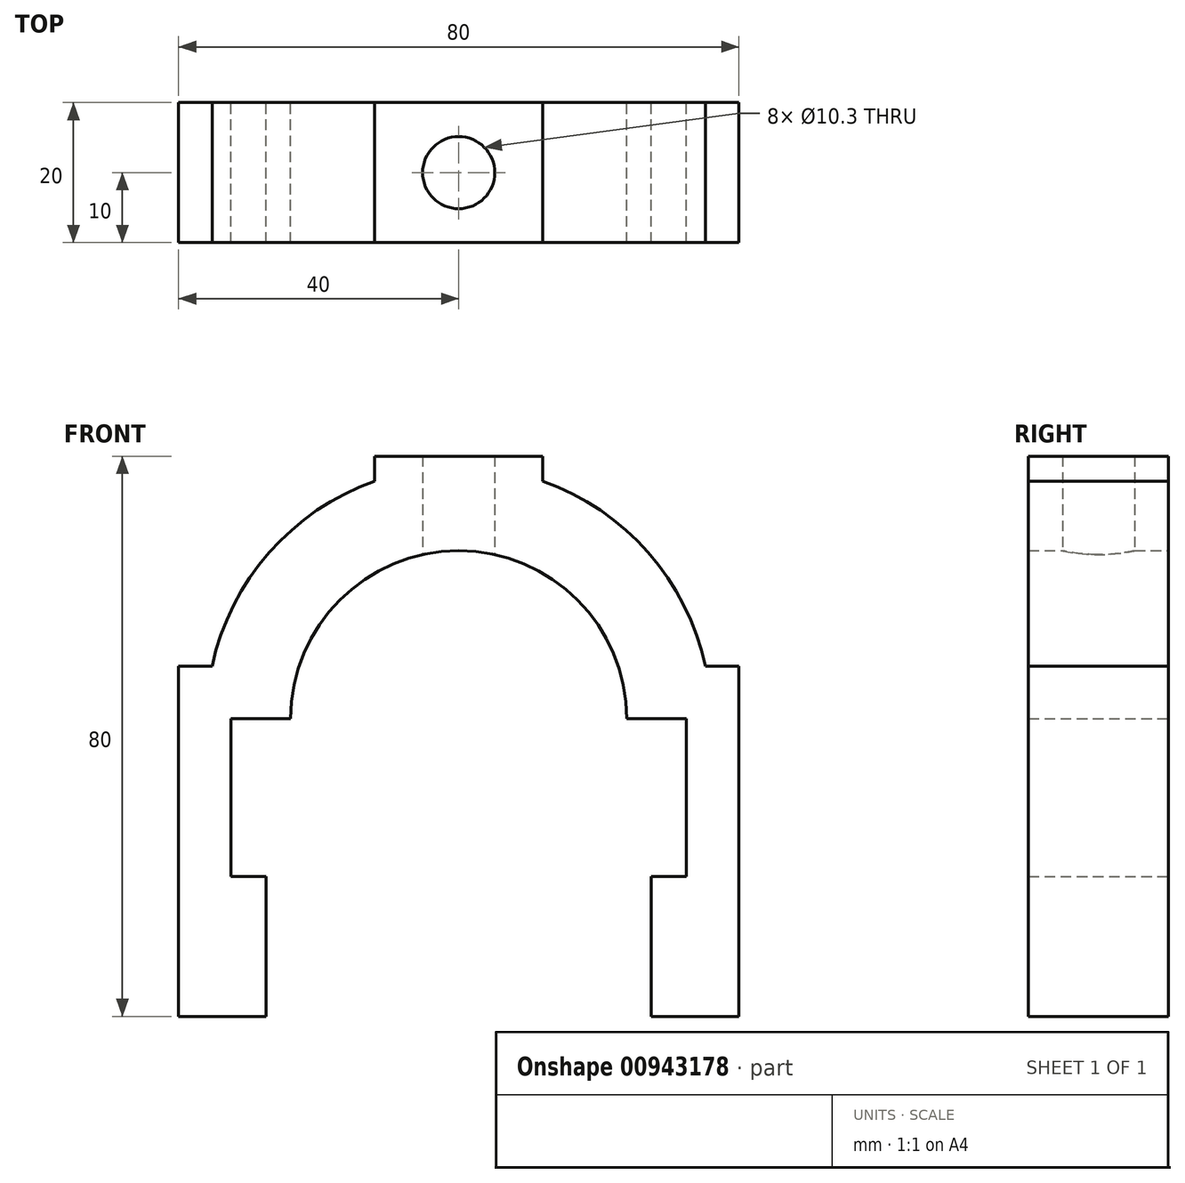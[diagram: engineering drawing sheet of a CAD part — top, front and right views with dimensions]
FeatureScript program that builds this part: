
annotation { "Feature Type Name" : "Feature", "Feature Type Description" : "" }
export const myFeature = defineFeature(function(context is Context, id is Id, definition is map)
    precondition{}
    {
        {
            var Q0;
            Q0=qCreatedBy(makeId("Front.planeOp"),FACE);
            var sketch = newSketch(context, id + "F0", { "sketchPlane" : qUnion([Q0])});
            skLineSegment(sketch, "E0", {"start": v(0, 51.15) * mm, "end": v(0, -47.63) * mm, "construction": true});
            skArc(sketch, "E1", {"start": v(-12, 33.94) * mm, "mid": v(-27.06, 23.75) * mm, "end": v(-35.21, 7.5) * mm});
            skArc(sketch, "E2", {"start": v(0, 24) * mm, "mid": v(-16.97, 16.97) * mm, "end": v(-24, 0) * mm});
            skLineSegment(sketch, "E3", {"start": v(-40, -42.5) * mm, "end": v(-27.5, -42.5) * mm});
            skLineSegment(sketch, "E4", {"start": v(-27.5, -42.5) * mm, "end": v(-27.5, -22.5) * mm});
            skLineSegment(sketch, "E5", {"start": v(-27.5, -22.5) * mm, "end": v(-32.5, -22.5) * mm});
            skLineSegment(sketch, "E6", {"start": v(-40, -42.5) * mm, "end": v(-40, 7.5) * mm});
            skLineSegment(sketch, "E7", {"start": v(-40, 7.5) * mm, "end": v(-35.21, 7.5) * mm});
            skLineSegment(sketch, "E8", {"start": v(-24, 0) * mm, "end": v(-32.5, 0) * mm});
            skLineSegment(sketch, "E9", {"start": v(-32.5, 0) * mm, "end": v(-32.5, -22.5) * mm});
            skLineSegment(sketch, "E10", {"start": v(-12, 33.94) * mm, "end": v(-12, 37.5) * mm});
            skLineSegment(sketch, "E11", {"start": v(-12, 37.5) * mm, "end": v(0, 37.5) * mm});
            skLineSegment(sketch, "E12.MirrorCS", {"start": v(40, -42.5) * mm, "end": v(27.5, -42.5) * mm});
            skLineSegment(sketch, "E13.MirrorCS", {"start": v(27.5, -42.5) * mm, "end": v(27.5, -22.5) * mm});
            skLineSegment(sketch, "E14.MirrorCS", {"start": v(27.5, -22.5) * mm, "end": v(32.5, -22.5) * mm});
            skLineSegment(sketch, "E15.MirrorCS", {"start": v(32.5, 0) * mm, "end": v(32.5, -22.5) * mm});
            skLineSegment(sketch, "E16.MirrorCS", {"start": v(24, 0) * mm, "end": v(32.5, 0) * mm});
            skArc(sketch, "E17.MirrorCS", {"start": v(0, 24) * mm, "mid": v(16.97, 16.97) * mm, "end": v(24, 0) * mm});
            skLineSegment(sketch, "E18.MirrorCS", {"start": v(12, 37.5) * mm, "end": v(0, 37.5) * mm});
            skLineSegment(sketch, "E19.MirrorCS", {"start": v(12, 33.94) * mm, "end": v(12, 37.5) * mm});
            skArc(sketch, "E20.MirrorCS", {"start": v(12, 33.94) * mm, "mid": v(27.06, 23.75) * mm, "end": v(35.21, 7.5) * mm});
            skLineSegment(sketch, "E21.MirrorCS", {"start": v(40, 7.5) * mm, "end": v(35.21, 7.5) * mm});
            skLineSegment(sketch, "E22.MirrorCS", {"start": v(40, -42.5) * mm, "end": v(40, 7.5) * mm});
            skSolve(sketch);
        }
        {
            var Q0;
            Q0=qSketchRegion(id+"F0",true);
            extrude(context, id + "F1", {"entities" : qUnion([Q0]), "depth" : 20 * mm, "offsetDistance" : 25 * mm, "symmetric" : true});
        }
        {
            var Q0;
            Q0=qCreatedBy(makeId("Top.planeOp"),FACE);
            var sketch = newSketch(context, id + "F2", { "sketchPlane" : qUnion([Q0])});
            skCircle(sketch, "E23", {"center": v(0, 0) * mm, "radius": 5.25 * mm});
            skSolve(sketch);
        }
        {
            var Q0;
            Q0=sQuery(id+"F2.wireOp",VERTEX,"E23.center");
            var Q1;
            Q1=makeQuery(id+"F1.opExtrude","SWEPT_BODY",BODY,{"disambiguationData":[OSD([sQuery(id+"F0.wireOp",EDGE,"E1"),sQuery(id+"F0.wireOp",EDGE,"E2"),sQuery(id+"F0.wireOp",EDGE,"E3"),sQuery(id+"F0.wireOp",EDGE,"E4"),sQuery(id+"F0.wireOp",EDGE,"E5"),sQuery(id+"F0.wireOp",EDGE,"E6"),sQuery(id+"F0.wireOp",EDGE,"E7"),sQuery(id+"F0.wireOp",EDGE,"E9"),sQuery(id+"F0.wireOp",EDGE,"E8"),sQuery(id+"F0.wireOp",EDGE,"E10"),sQuery(id+"F0.wireOp",EDGE,"E11"),sQuery(id+"F0.wireOp",EDGE,"E12.MirrorCS"),sQuery(id+"F0.wireOp",EDGE,"E13.MirrorCS"),sQuery(id+"F0.wireOp",EDGE,"E14.MirrorCS"),sQuery(id+"F0.wireOp",EDGE,"E15.MirrorCS"),sQuery(id+"F0.wireOp",EDGE,"E16.MirrorCS"),sQuery(id+"F0.wireOp",EDGE,"E17.MirrorCS"),sQuery(id+"F0.wireOp",EDGE,"E18.MirrorCS"),sQuery(id+"F0.wireOp",EDGE,"E19.MirrorCS"),sQuery(id+"F0.wireOp",EDGE,"E20.MirrorCS"),sQuery(id+"F0.wireOp",EDGE,"E21.MirrorCS"),sQuery(id+"F0.wireOp",EDGE,"E22.MirrorCS")])]});
            hole(context, id + "F3", {"style" : HoleStyle.SIMPLE, "endStyle" : HoleEndStyle.THROUGH, "oppositeDirection" : true, "standardTappedOrClearance" : lookupTablePath({ "standard" : "ISO", "engagement" : "75%", "pitch" : "1.75 mm", "size" : "M12", "type" : "Tapped" }), "standardBlindInLast" : lookupTablePath({ "standard" : "ISO", "fit" : "Normal", "engagement" : "75%", "pitch" : "1.75 mm", "size" : "M12", "type" : "Clearance & tapped" }), "holeDiameter" : 10.3 * mm, "majorDiameter" : 12 * mm, "showTappedDepth" : true, "isTappedThrough" : true, "tappedDepth" : 12 * mm, "tapClearance" : 3, "locations" : qUnion([Q0]), "scope" : qUnion([Q1])});
        }
    });
